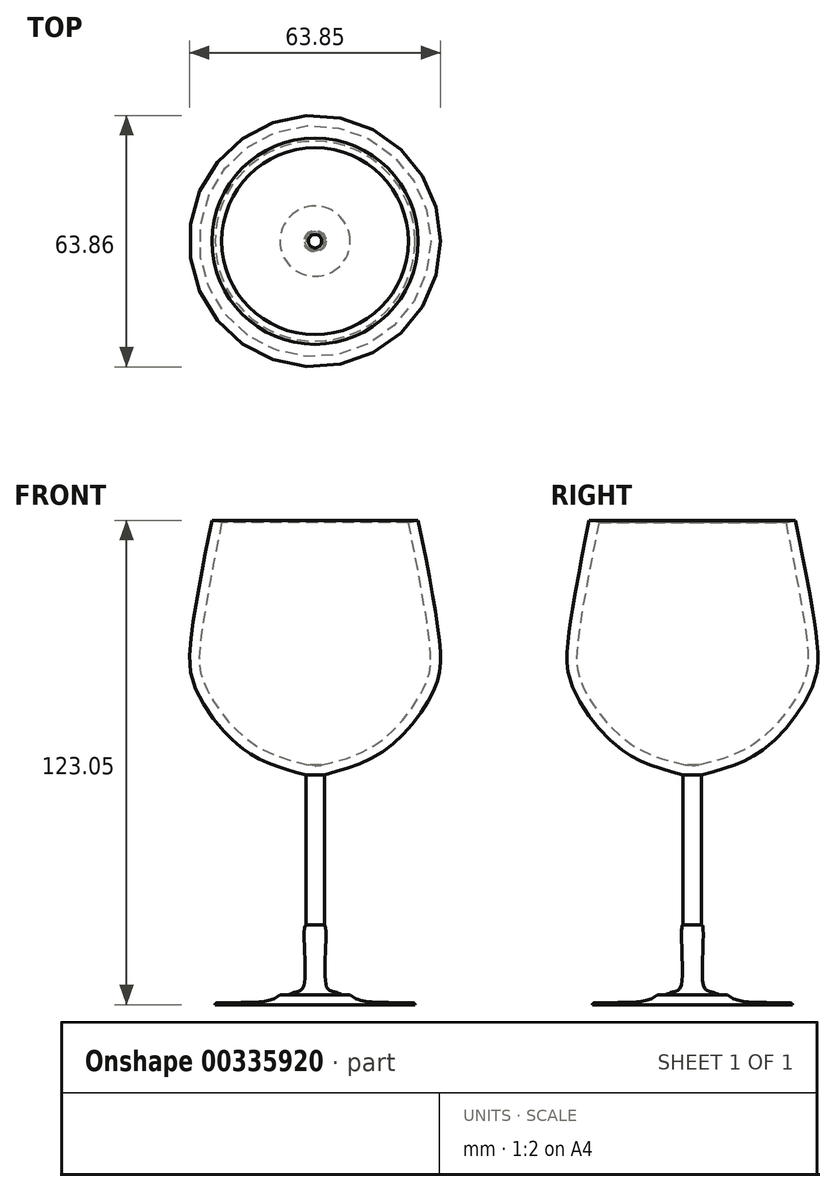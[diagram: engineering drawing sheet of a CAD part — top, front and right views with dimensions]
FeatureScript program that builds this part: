
annotation { "Feature Type Name" : "Feature", "Feature Type Description" : "" }
export const myFeature = defineFeature(function(context is Context, id is Id, definition is map)
    precondition{}
    {
        {
            var Q0;
            Q0=qCreatedBy(makeId("Front.planeOp"),FACE);
            var sketch = newSketch(context, id + "F0", { "sketchPlane" : qUnion([Q0])});
            skLineSegment(sketch, "E0", {"start": v(0, 0) * mm, "end": v(25.4, 0) * mm});
            skLineSegment(sketch, "E1", {"start": v(8.92, 2.54) * mm, "end": v(8.92, 2.93) * mm});
            skLineSegment(sketch, "E2", {"start": v(2.36, 20.31) * mm, "end": v(2.36, 58.41) * mm});
            skFitSpline(sketch, "E3", {"points": [v(2.36, 58.41) * mm, v(18.29, 65) * mm, v(30.36, 80.35) * mm, v(31.75, 91.16) * mm, v(26.21, 123.05) * mm], "startDerivative": vector(69.65, 18.35) * mm, "endDerivative": vector(-22.44, 112.87) * mm});
            skFitSpline(sketch, "E4.0", {"points": [v(1.7, 60.87) * mm, v(3.16, 61.25) * mm, v(6.01, 62) * mm, v(10.1, 63.34) * mm, v(13.31, 64.8) * mm, v(15.76, 66.29) * mm, v(17.54, 67.6) * mm, v(19.3, 69.15) * mm, v(21.57, 71.44) * mm, v(23.65, 74) * mm, v(25.44, 76.59) * mm, v(26.61, 78.5) * mm, v(27.42, 80.03) * mm, v(27.96, 81.18) * mm, v(28.41, 82.26) * mm, v(28.84, 83.5) * mm, v(29.17, 84.9) * mm, v(29.35, 86.31) * mm, v(29.4, 87.86) * mm, v(29.35, 89.33) * mm, v(29.25, 90.64) * mm, v(29.11, 92.06) * mm, v(28.88, 94) * mm, v(28.52, 96.58) * mm, v(28.1, 99.36) * mm, v(27.42, 103.33) * mm, v(26.45, 108.67) * mm, v(25.12, 115.5) * mm, v(24.19, 120.2) * mm, v(23.72, 122.56) * mm]});
            skLineSegment(sketch, "E5", {"start": v(26.21, 123.05) * mm, "end": v(23.72, 122.56) * mm});
            skLineSegment(sketch, "E6", {"start": v(1.7, 60.87) * mm, "end": v(0, 60.68) * mm});
            skLineSegment(sketch, "E7", {"start": v(0, 60.68) * mm, "end": v(0, 0) * mm});
            skPoint(sketch, "E8.visualSharp", {"position": v(8.92, 5.47) * mm});
            skArc(sketch, "E8.filletArc", {"start": v(8.92, 5.17) * mm, "mid": v(8.83, 5.38) * mm, "end": v(8.62, 5.47) * mm});
            skFitSpline(sketch, "E9", {"points": [v(8.92, 2.54) * mm, v(11.3, 1.17) * mm, v(18.49, 0.53) * mm, v(25.38, 0.45) * mm], "startDerivative": vector(8.2, -6.51) * mm, "endDerivative": vector(17.47, -0.14) * mm});
            skLineSegment(sketch, "E10", {"start": v(25.4, 0) * mm, "end": v(25.38, 0.45) * mm});
            skFitSpline(sketch, "E11", {"points": [v(2.36, 20.31) * mm, v(2.82, 4.9) * mm, v(4.88, 3.24) * mm, v(7.64, 2.38) * mm, v(8.92, 2.54) * mm], "startDerivative": vector(7.02, -1.69) * mm, "endDerivative": vector(5.75, 1.37) * mm});
            skSolve(sketch);
        }
        {
            var Q0;
            Q0=makeQuery(id+"F0.imprint","IMPRINT",FACE,{"disambiguationData":[TD([[makeQuery(id+"F0.imprint","IMPRINT",EDGE,{"derivedFrom":sQuery(id+"F0.wireOp",EDGE,"E0")}),1.0]])]});
            var Q1;
            Q1=sQuery(id+"F0.wireOp",EDGE,"E7");
            revolve(context, id + "F1", {"entities" : qUnion([Q0]), "axis" : qUnion([Q1]), "revolveType" : RevolveType.FULL});
        }
        {
            var Q0;
            Q0=makeQuery(id+"F1.opRevolve","SWEPT_EDGE",EDGE,{"disambiguationData":[OSD([sQuery(id+"F0.wireOp",EDGE,"E9"),sQuery(id+"F0.wireOp",EDGE,"E10")])]});
            fillet(context, id + "F2", {"entities" : qUnion([Q0]), "radius" : 0.5 * mm, "tangentPropagation" : true, "allowEdgeOverflow" : false});
        }
    });
